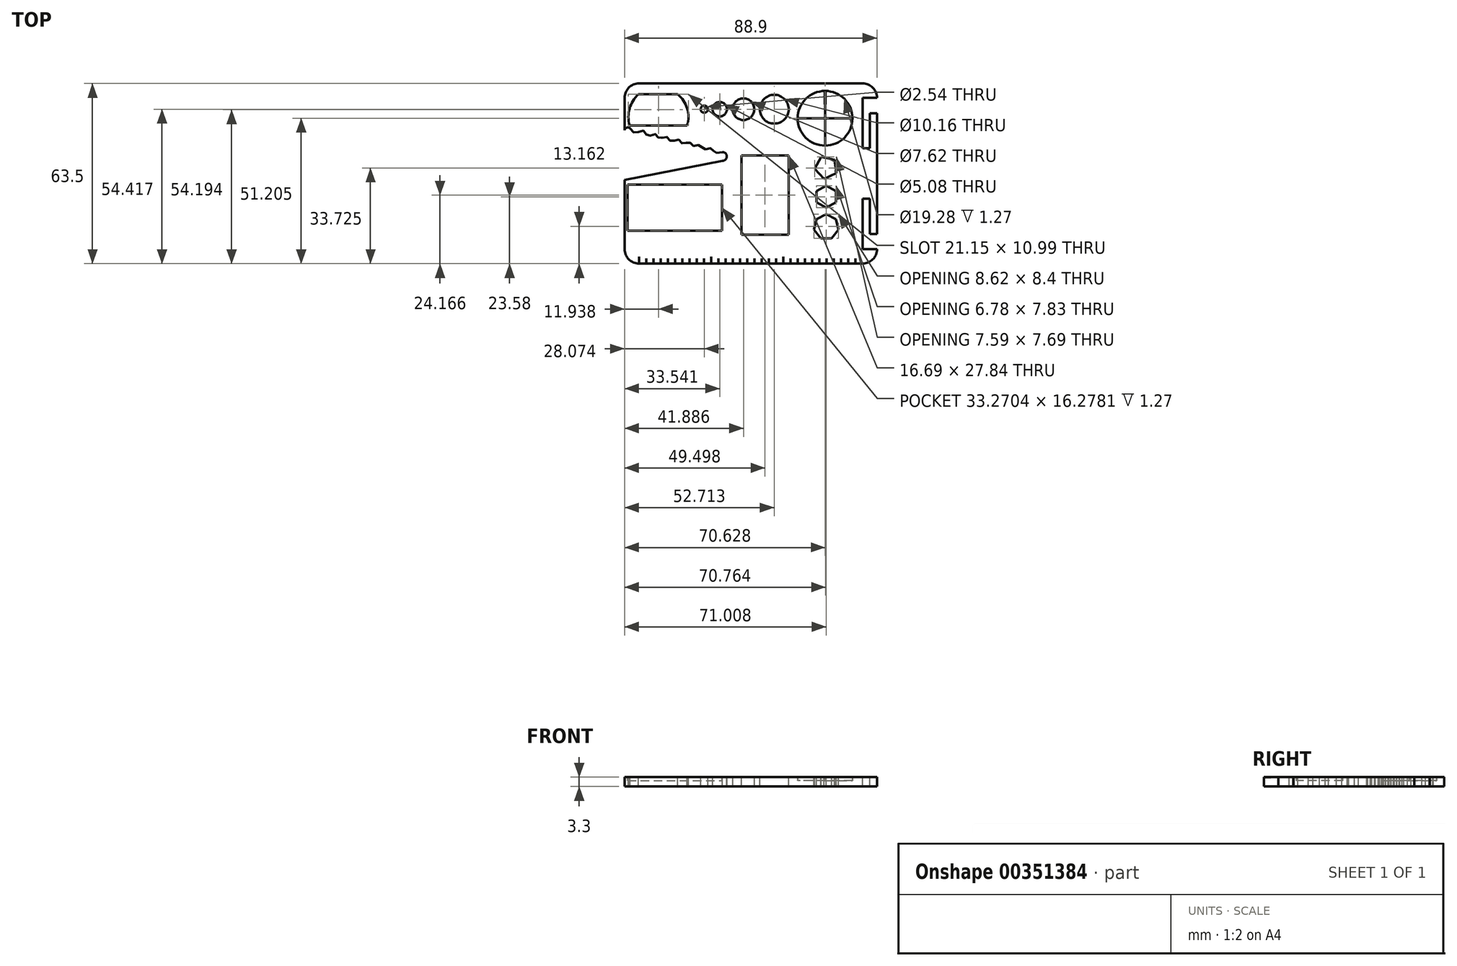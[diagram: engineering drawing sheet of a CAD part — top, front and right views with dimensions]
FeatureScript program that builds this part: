
annotation { "Feature Type Name" : "Feature", "Feature Type Description" : "" }
export const myFeature = defineFeature(function(context is Context, id is Id, definition is map)
    precondition{}
    {
        {
            var Q0;
            Q0=qCreatedBy(makeId("Top.planeOp"),FACE);
            var sketch = newSketch(context, id + "F0", { "sketchPlane" : qUnion([Q0])});
            skLineSegment(sketch, "E0", {"start": v(0, 0) * mm, "end": v(88.9, 0) * mm});
            skLineSegment(sketch, "E1", {"start": v(88.9, 0) * mm, "end": v(88.9, 63.5) * mm});
            skLineSegment(sketch, "E2", {"start": v(88.9, 63.5) * mm, "end": v(0, 63.5) * mm});
            skLineSegment(sketch, "E3", {"start": v(0, 63.5) * mm, "end": v(0, 0) * mm});
            skSolve(sketch);
        }
        {
            var Q0;
            Q0 = qSketchRegion(id + "F0", true);
            extrude(context, id + "F1", {"entities" : qUnion([Q0]), "depth" : 3.3 * mm});
        }
        {
            var Q0;
            Q0=makeQuery(id+"F1.opExtrude","CAP_FACE",FACE,{"disambiguationData":[OSD([sQuery(id+"F0.wireOp",EDGE,"E0"),sQuery(id+"F0.wireOp",EDGE,"E1"),sQuery(id+"F0.wireOp",EDGE,"E2"),sQuery(id+"F0.wireOp",EDGE,"E3")])],"isStart":false});
            var sketch = newSketch(context, id + "F2", { "sketchPlane" : qUnion([Q0])});
            skLineSegment(sketch, "E4", {"start": v(5.08, 0) * mm, "end": v(5.08, 2.43) * mm});
            skLineSegment(sketch, "E5", {"start": v(5.08, 2.43) * mm, "end": v(5.1, 2.43) * mm});
            skLineSegment(sketch, "E6", {"start": v(5.1, 2.43) * mm, "end": v(5.1, 0) * mm});
            skLineSegment(sketch, "E7", {"start": v(5.1, 0) * mm, "end": v(7.65, 0) * mm});
            skLineSegment(sketch, "E8", {"start": v(7.65, 0) * mm, "end": v(7.65, 1.82) * mm});
            skLineSegment(sketch, "E9", {"start": v(0, 0) * mm, "end": v(5.08, 0) * mm});
            skLineSegment(sketch, "E10", {"start": v(7.65, 1.82) * mm, "end": v(7.62, 1.82) * mm});
            skLineSegment(sketch, "E11", {"start": v(7.62, 1.82) * mm, "end": v(7.62, 0) * mm});
            skLineSegment(sketch, "E12", {"start": v(7.62, 0) * mm, "end": v(10.16, 0) * mm});
            skLineSegment(sketch, "E13", {"start": v(10.16, 0) * mm, "end": v(10.16, 1.82) * mm});
            skLineSegment(sketch, "E14", {"start": v(10.16, 1.82) * mm, "end": v(10.19, 1.82) * mm});
            skLineSegment(sketch, "E15", {"start": v(10.19, 1.82) * mm, "end": v(10.19, 0) * mm});
            skLineSegment(sketch, "E16", {"start": v(10.16, 0) * mm, "end": v(12.7, 0) * mm});
            skLineSegment(sketch, "E17", {"start": v(12.7, 0) * mm, "end": v(12.7, 1.82) * mm});
            skLineSegment(sketch, "E18", {"start": v(12.7, 1.82) * mm, "end": v(12.73, 1.82) * mm});
            skLineSegment(sketch, "E19", {"start": v(12.73, 1.82) * mm, "end": v(12.73, 0) * mm});
            skLineSegment(sketch, "E20.0", {"start": v(15.24, 0) * mm, "end": v(15.24, 1.82) * mm});
            skLineSegment(sketch, "E21.0", {"start": v(17.78, 0) * mm, "end": v(17.78, 1.82) * mm});
            skLineSegment(sketch, "E22.0", {"start": v(20.32, 0) * mm, "end": v(20.32, 1.82) * mm});
            skLineSegment(sketch, "E23.0", {"start": v(22.86, 0) * mm, "end": v(22.86, 1.82) * mm});
            skLineSegment(sketch, "E24.0", {"start": v(25.4, 0) * mm, "end": v(25.4, 1.82) * mm});
            skLineSegment(sketch, "E25.0", {"start": v(27.94, 0) * mm, "end": v(27.94, 1.82) * mm});
            skLineSegment(sketch, "E26.0", {"start": v(30.48, 0) * mm, "end": v(30.48, 2.43) * mm});
            skLineSegment(sketch, "E27.0", {"start": v(33.02, 0) * mm, "end": v(33.02, 1.82) * mm});
            skLineSegment(sketch, "E28.0", {"start": v(35.56, 0) * mm, "end": v(35.56, 1.82) * mm});
            skLineSegment(sketch, "E29.0", {"start": v(38.1, 0) * mm, "end": v(38.1, 1.82) * mm});
            skLineSegment(sketch, "E30.0", {"start": v(40.64, 0) * mm, "end": v(40.64, 1.82) * mm});
            skLineSegment(sketch, "E31.0", {"start": v(43.18, 0) * mm, "end": v(43.18, 1.82) * mm});
            skLineSegment(sketch, "E32.0", {"start": v(45.72, 0) * mm, "end": v(45.72, 1.82) * mm});
            skLineSegment(sketch, "E33.0", {"start": v(48.26, 0) * mm, "end": v(48.26, 1.82) * mm});
            skLineSegment(sketch, "E34.0", {"start": v(50.8, 0) * mm, "end": v(50.8, 1.82) * mm});
            skLineSegment(sketch, "E35.0", {"start": v(53.34, 0) * mm, "end": v(53.34, 1.82) * mm});
            skLineSegment(sketch, "E36.0", {"start": v(58.42, 0) * mm, "end": v(58.42, 1.82) * mm});
            skLineSegment(sketch, "E37.0", {"start": v(60.96, 0) * mm, "end": v(60.96, 1.82) * mm});
            skLineSegment(sketch, "E38.0", {"start": v(63.5, 0) * mm, "end": v(63.5, 1.82) * mm});
            skLineSegment(sketch, "E39.0", {"start": v(66.04, 0) * mm, "end": v(66.04, 1.82) * mm});
            skLineSegment(sketch, "E40.0", {"start": v(68.58, 0) * mm, "end": v(68.58, 1.82) * mm});
            skLineSegment(sketch, "E41.0", {"start": v(71.12, 0) * mm, "end": v(71.12, 1.82) * mm});
            skLineSegment(sketch, "E42.0", {"start": v(73.66, 0) * mm, "end": v(73.66, 1.82) * mm});
            skLineSegment(sketch, "E43.0", {"start": v(76.2, 0) * mm, "end": v(76.2, 1.82) * mm});
            skLineSegment(sketch, "E44.0", {"start": v(78.74, 0) * mm, "end": v(78.74, 1.82) * mm});
            skLineSegment(sketch, "E45.0", {"start": v(81.28, 0) * mm, "end": v(81.28, 1.82) * mm});
            skLineSegment(sketch, "E46.0", {"start": v(55.88, 0) * mm, "end": v(55.88, 2.43) * mm});
            skLineSegment(sketch, "E47.0", {"start": v(15.27, 1.82) * mm, "end": v(15.27, 0) * mm});
            skLineSegment(sketch, "E48.0", {"start": v(17.8, 1.82) * mm, "end": v(17.8, 0) * mm});
            skLineSegment(sketch, "E49.0", {"start": v(20.35, 1.82) * mm, "end": v(20.35, 0) * mm});
            skLineSegment(sketch, "E50.0", {"start": v(22.89, 1.82) * mm, "end": v(22.89, 0) * mm});
            skLineSegment(sketch, "E51.0", {"start": v(25.43, 1.82) * mm, "end": v(25.43, 0) * mm});
            skLineSegment(sketch, "E52.0", {"start": v(27.97, 1.82) * mm, "end": v(27.97, 0) * mm});
            skLineSegment(sketch, "E53.0", {"start": v(30.5, 1.82) * mm, "end": v(30.5, 0) * mm});
            skLineSegment(sketch, "E54.0", {"start": v(33.05, 1.82) * mm, "end": v(33.05, 0) * mm});
            skLineSegment(sketch, "E55.0", {"start": v(35.59, 1.82) * mm, "end": v(35.59, 0) * mm});
            skLineSegment(sketch, "E56.0", {"start": v(38.13, 1.82) * mm, "end": v(38.13, 0) * mm});
            skLineSegment(sketch, "E57.0", {"start": v(40.67, 1.82) * mm, "end": v(40.67, 0) * mm});
            skLineSegment(sketch, "E58.0", {"start": v(43.2, 1.82) * mm, "end": v(43.2, 0) * mm});
            skLineSegment(sketch, "E59.0", {"start": v(45.75, 1.82) * mm, "end": v(45.75, 0) * mm});
            skLineSegment(sketch, "E60.0", {"start": v(48.29, 1.82) * mm, "end": v(48.29, 0) * mm});
            skLineSegment(sketch, "E61.0", {"start": v(50.83, 1.82) * mm, "end": v(50.83, 0) * mm});
            skLineSegment(sketch, "E62.0", {"start": v(53.37, 1.82) * mm, "end": v(53.37, 0) * mm});
            skLineSegment(sketch, "E63.0", {"start": v(55.9, 1.82) * mm, "end": v(55.9, 0) * mm});
            skLineSegment(sketch, "E64.0", {"start": v(58.45, 1.82) * mm, "end": v(58.45, 0) * mm});
            skLineSegment(sketch, "E65.0", {"start": v(60.99, 1.82) * mm, "end": v(60.99, 0) * mm});
            skLineSegment(sketch, "E66.0", {"start": v(63.53, 1.82) * mm, "end": v(63.53, 0) * mm});
            skLineSegment(sketch, "E67.0", {"start": v(66.07, 1.82) * mm, "end": v(66.07, 0) * mm});
            skLineSegment(sketch, "E68.0", {"start": v(68.6, 1.82) * mm, "end": v(68.6, 0) * mm});
            skLineSegment(sketch, "E69.0", {"start": v(71.15, 1.82) * mm, "end": v(71.15, 0) * mm});
            skLineSegment(sketch, "E70.0", {"start": v(73.69, 1.82) * mm, "end": v(73.69, 0) * mm});
            skLineSegment(sketch, "E71.0", {"start": v(76.23, 1.82) * mm, "end": v(76.23, 0) * mm});
            skLineSegment(sketch, "E72.0", {"start": v(78.77, 1.82) * mm, "end": v(78.77, 0) * mm});
            skLineSegment(sketch, "E73.0", {"start": v(81.3, 1.82) * mm, "end": v(81.3, 0) * mm});
            skLineSegment(sketch, "E74", {"start": v(15.24, 1.82) * mm, "end": v(15.27, 1.82) * mm});
            skLineSegment(sketch, "E75.trimOffspring", {"start": v(81.28, 1.82) * mm, "end": v(81.3, 1.82) * mm});
            skLineSegment(sketch, "E76.trimOffspring", {"start": v(78.74, 1.82) * mm, "end": v(78.77, 1.82) * mm});
            skLineSegment(sketch, "E77.trimOffspring", {"start": v(76.2, 1.82) * mm, "end": v(76.23, 1.82) * mm});
            skLineSegment(sketch, "E78.trimOffspring", {"start": v(73.66, 1.82) * mm, "end": v(73.69, 1.82) * mm});
            skLineSegment(sketch, "E79.trimOffspring", {"start": v(71.12, 1.82) * mm, "end": v(71.15, 1.82) * mm});
            skLineSegment(sketch, "E80.trimOffspring", {"start": v(68.58, 1.82) * mm, "end": v(68.6, 1.82) * mm});
            skLineSegment(sketch, "E81.trimOffspring", {"start": v(66.04, 1.82) * mm, "end": v(66.07, 1.82) * mm});
            skLineSegment(sketch, "E82.trimOffspring", {"start": v(63.5, 1.82) * mm, "end": v(63.53, 1.82) * mm});
            skLineSegment(sketch, "E83.trimOffspring", {"start": v(60.96, 1.82) * mm, "end": v(60.99, 1.82) * mm});
            skLineSegment(sketch, "E84.trimOffspring", {"start": v(58.42, 1.82) * mm, "end": v(58.45, 1.82) * mm});
            skLineSegment(sketch, "E85", {"start": v(55.9, 1.82) * mm, "end": v(55.9, 2.43) * mm});
            skLineSegment(sketch, "E86", {"start": v(55.9, 2.43) * mm, "end": v(55.88, 2.43) * mm});
            skLineSegment(sketch, "E87.trimOffspring", {"start": v(53.34, 1.82) * mm, "end": v(53.37, 1.82) * mm});
            skLineSegment(sketch, "E88.trimOffspring", {"start": v(50.8, 1.82) * mm, "end": v(50.83, 1.82) * mm});
            skLineSegment(sketch, "E89.trimOffspring", {"start": v(48.26, 1.82) * mm, "end": v(48.29, 1.82) * mm});
            skLineSegment(sketch, "E90.trimOffspring", {"start": v(45.72, 1.82) * mm, "end": v(45.75, 1.82) * mm});
            skLineSegment(sketch, "E91.trimOffspring", {"start": v(43.18, 1.82) * mm, "end": v(43.2, 1.82) * mm});
            skLineSegment(sketch, "E92.trimOffspring", {"start": v(40.64, 1.82) * mm, "end": v(40.67, 1.82) * mm});
            skLineSegment(sketch, "E93.trimOffspring", {"start": v(38.1, 1.82) * mm, "end": v(38.13, 1.82) * mm});
            skLineSegment(sketch, "E94.trimOffspring", {"start": v(35.56, 1.82) * mm, "end": v(35.59, 1.82) * mm});
            skLineSegment(sketch, "E95.trimOffspring", {"start": v(33.02, 1.82) * mm, "end": v(33.05, 1.82) * mm});
            skLineSegment(sketch, "E96.trimOffspring", {"start": v(17.78, 1.82) * mm, "end": v(17.8, 1.82) * mm});
            skLineSegment(sketch, "E97.trimOffspring", {"start": v(20.32, 1.82) * mm, "end": v(20.35, 1.82) * mm});
            skLineSegment(sketch, "E98.trimOffspring", {"start": v(22.86, 1.82) * mm, "end": v(22.89, 1.82) * mm});
            skLineSegment(sketch, "E99.trimOffspring", {"start": v(27.94, 1.82) * mm, "end": v(27.97, 1.82) * mm});
            skLineSegment(sketch, "E100", {"start": v(30.48, 2.43) * mm, "end": v(30.5, 2.43) * mm});
            skLineSegment(sketch, "E101", {"start": v(30.5, 2.43) * mm, "end": v(30.5, 1.82) * mm});
            skLineSegment(sketch, "E102", {"start": v(5.08, 0) * mm, "end": v(81.3, 0) * mm});
            skLineSegment(sketch, "E103", {"start": v(25.4, 1.82) * mm, "end": v(25.43, 1.82) * mm});
            skLineSegment(sketch, "E104", {"start": v(4.86, 59.7) * mm, "end": v(18.65, 59.7) * mm});
            skArc(sketch, "E105", {"start": v(22.06, 48.7) * mm, "mid": v(22.05, 54.72) * mm, "end": v(18.65, 59.7) * mm});
            skArc(sketch, "E106", {"start": v(4.86, 59.7) * mm, "mid": v(1.77, 54.63) * mm, "end": v(1.78, 48.7) * mm});
            skLineSegment(sketch, "E107", {"start": v(1.78, 48.7) * mm, "end": v(22.06, 48.7) * mm});
            skSolve(sketch);
        }
        {
            var Q0;
            Q0=makeQuery(id+"F1.opExtrude","SWEPT_EDGE",EDGE,{"disambiguationData":[OSD([sQuery(id+"F0.wireOp",EDGE,"E0"),sQuery(id+"F0.wireOp",EDGE,"E3")])]});
            var Q1;
            Q1=makeQuery(id+"F1.opExtrude","SWEPT_EDGE",EDGE,{"disambiguationData":[OSD([sQuery(id+"F0.wireOp",EDGE,"E0"),sQuery(id+"F0.wireOp",EDGE,"E1")])]});
            var Q2;
            Q2=makeQuery(id+"F1.opExtrude","SWEPT_EDGE",EDGE,{"disambiguationData":[OSD([sQuery(id+"F0.wireOp",EDGE,"E1"),sQuery(id+"F0.wireOp",EDGE,"E2")])]});
            var Q3;
            Q3=makeQuery(id+"F1.opExtrude","SWEPT_EDGE",EDGE,{"disambiguationData":[OSD([sQuery(id+"F0.wireOp",EDGE,"E2"),sQuery(id+"F0.wireOp",EDGE,"E3")])]});
            fillet(context, id + "F3", {"entities" : qUnion([Q0, Q1, Q2, Q3]), "radius" : 5.08 * mm, "tangentPropagation" : true, "allowEdgeOverflow" : false});
        }
        {
            var Q0;
            Q0 = qSketchRegion(id + "F2", true);
            extrude(context, id + "F4", {"entities" : qUnion([Q0]), "operationType" : NewBodyOperationType.REMOVE, "oppositeDirection" : true, "depth" : 0.25 * mm});
        }
        {
            var Q0;
            Q0=makeQuery(id+"F1.opExtrude","CAP_FACE",FACE,{"disambiguationData":[OSD([sQuery(id+"F0.wireOp",EDGE,"E0"),sQuery(id+"F0.wireOp",EDGE,"E1"),sQuery(id+"F0.wireOp",EDGE,"E2"),sQuery(id+"F0.wireOp",EDGE,"E3")])],"isStart":false});
            var sketch = newSketch(context, id + "F5", { "sketchPlane" : qUnion([Q0])});
            skCircle(sketch, "E108", {"center": v(28.07, 54.42) * mm, "radius": 1.27 * mm});
            skCircle(sketch, "E109", {"center": v(33.54, 54.42) * mm, "radius": 2.54 * mm});
            skCircle(sketch, "E110", {"center": v(41.89, 54.42) * mm, "radius": 3.81 * mm});
            skCircle(sketch, "E111", {"center": v(52.71, 54.42) * mm, "radius": 5.08 * mm});
            skArc(sketch, "E112.0", {"start": v(4.86, 59.7) * mm, "mid": v(1.77, 54.63) * mm, "end": v(1.78, 48.7) * mm});
            skLineSegment(sketch, "E113.0", {"start": v(4.86, 59.7) * mm, "end": v(18.65, 59.7) * mm});
            skArc(sketch, "E114.0", {"start": v(22.06, 48.7) * mm, "mid": v(22.05, 54.72) * mm, "end": v(18.65, 59.7) * mm});
            skLineSegment(sketch, "E115.0", {"start": v(1.78, 48.7) * mm, "end": v(22.06, 48.7) * mm});
            skSolve(sketch);
        }
        {
            var Q0;
            Q0 = qSketchRegion(id + "F5", true);
            extrude(context, id + "F6", {"entities" : qUnion([Q0]), "operationType" : NewBodyOperationType.REMOVE, "oppositeDirection" : true, "depth" : 25.4 * mm});
        }
        {
            var Q0;
            Q0=makeQuery(id+"F1.opExtrude","SWEPT_FACE",FACE,{"disambiguationData":[OSD([sQuery(id+"F0.wireOp",EDGE,"E1")])]});
            var sketch = newSketch(context, id + "F7", { "sketchPlane" : qUnion([Q0])});
            skLineSegment(sketch, "E116.0", {"start": v(5.08, 3.3) * mm, "end": v(5.08, 0) * mm});
            skLineSegment(sketch, "E117.0", {"start": v(5.08, 3.3) * mm, "end": v(58.42, 3.3) * mm});
            skLineSegment(sketch, "E118.0", {"start": v(58.42, 0) * mm, "end": v(58.42, 3.3) * mm});
            skLineSegment(sketch, "E119.0", {"start": v(5.08, 0) * mm, "end": v(58.42, 0) * mm});
            skSolve(sketch);
        }
        {
            var Q0;
            Q0 = qSketchRegion(id + "F7", true);
            extrude(context, id + "F8", {"entities" : qUnion([Q0]), "operationType" : NewBodyOperationType.REMOVE, "oppositeDirection" : true, "depth" : 5.08 * mm});
        }
        {
            var Q0;
            Q0=makeQuery(id+"F8.boolean.opBoolean","COPY",FACE,{"derivedFrom":makeQuery(id+"F8.opExtrude","CAP_FACE",FACE,{"disambiguationData":[OSD([sQuery(id+"F7.wireOp",EDGE,"E116.0"),sQuery(id+"F7.wireOp",EDGE,"E117.0"),sQuery(id+"F7.wireOp",EDGE,"E118.0"),sQuery(id+"F7.wireOp",EDGE,"E119.0")])],"isStart":false})});
            var sketch = newSketch(context, id + "F9", { "sketchPlane" : qUnion([Q0])});
            skPoint(sketch, "E120.startSnap0", {"position": v(5.08, 1.65) * mm});
            skPoint(sketch, "E120.startSnap1", {"position": v(31.75, 0) * mm});
            skLineSegment(sketch, "E121", {"start": v(22.86, 0) * mm, "end": v(22.86, 3.3) * mm});
            skLineSegment(sketch, "E122", {"start": v(40.64, 3.3) * mm, "end": v(22.86, 3.3) * mm});
            skLineSegment(sketch, "E123", {"start": v(40.64, 3.3) * mm, "end": v(40.64, 0) * mm});
            skLineSegment(sketch, "E124", {"start": v(40.64, 0) * mm, "end": v(22.86, 0) * mm});
            skSolve(sketch);
        }
        {
            var Q0;
            Q0 = qSketchRegion(id + "F9", true);
            extrude(context, id + "F10", {"entities" : qUnion([Q0]), "operationType" : NewBodyOperationType.ADD, "depth" : 2.54 * mm});
        }
        {
            var Q0;
            {var subQ0=sQuery(id+"F0.wireOp",EDGE,"E3");var subQ1=sQuery(id+"F0.wireOp",EDGE,"E2");var subQ2=sQuery(id+"F0.wireOp",EDGE,"E1");Q0=makeQuery(id+"Fheyj9GnmQKfGOX_1.boolean.opBoolean","SPLIT",FACE,{"disambiguationData":[TD([makeQuery(id+"F1.opExtrude","SWEPT_FACE",FACE,{"disambiguationData":[OSD([subQ1])]})])],"derivedFrom":makeQuery(id+"F1.opExtrude","CAP_FACE",FACE,{"disambiguationData":[OSD([sQuery(id+"F0.wireOp",EDGE,"E0"),subQ2,subQ1,subQ0])],"isStart":false})});}
            var sketch = newSketch(context, id + "F11", { "sketchPlane" : qUnion([Q0])});
            skLineSegment(sketch, "E125", {"start": v(34.47, 36.23) * mm, "end": v(0, 29.44) * mm});
            skArc(sketch, "E126", {"start": v(34.47, 36.23) * mm, "mid": v(36.01, 37.77) * mm, "end": v(34.47, 39.32) * mm});
            skFitSpline(sketch, "E127", {"points": [v(34.47, 39.32) * mm, v(31.6, 39.32) * mm, v(30.46, 40.69) * mm, v(27.95, 40.38) * mm, v(26.5, 41.74) * mm, v(24.3, 41.5) * mm, v(22.66, 42.85) * mm, v(20.42, 42.29) * mm, v(18.81, 43.75) * mm, v(16.53, 42.98) * mm, v(14.76, 44.7) * mm, v(12.26, 44.12) * mm, v(10.92, 45.6) * mm, v(8.2, 44.96) * mm, v(6.7, 46.8) * mm, v(3.93, 46.06) * mm, v(1.95, 47.66) * mm], "startDerivative": vector(-49.51, -10.48) * mm, "endDerivative": vector(-26.38, 38.01) * mm});
            skArc(sketch, "E128", {"start": v(1.95, 47.66) * mm, "mid": v(0.77, 47.9) * mm, "end": v(0, 46.96) * mm});
            skLineSegment(sketch, "E129", {"start": v(0, 46.96) * mm, "end": v(0, 29.44) * mm});
            skSolve(sketch);
        }
        {
            var Q0;
            Q0 = qSketchRegion(id + "F11", true);
            extrude(context, id + "F12", {"entities" : qUnion([Q0]), "operationType" : NewBodyOperationType.REMOVE, "oppositeDirection" : true, "depth" : 25.4 * mm});
        }
        {
            var Q0;
            {var subQ9=sQuery(id+"F0.wireOp",EDGE,"E3");var subQ10=sQuery(id+"F0.wireOp",EDGE,"E2");var subQ13=makeQuery(id+"F1.opExtrude","SWEPT_FACE",FACE,{"disambiguationData":[OSD([subQ10])]});var subQ18=sQuery(id+"F0.wireOp",EDGE,"E1");Q0=makeQuery(id+"FrTG45sfuEWpLZh_1.boolean.opBoolean","SPLIT",FACE,{"disambiguationData":[TD([subQ13])],"derivedFrom":makeQuery(id+"Fheyj9GnmQKfGOX_1.boolean.opBoolean","SPLIT",FACE,{"disambiguationData":[TD([subQ13])],"derivedFrom":makeQuery(id+"F1.opExtrude","CAP_FACE",FACE,{"disambiguationData":[OSD([sQuery(id+"F0.wireOp",EDGE,"E0"),subQ18,subQ10,subQ9])],"isStart":false})})});}
            var sketch = newSketch(context, id + "F13", { "sketchPlane" : qUnion([Q0])});
            skCircle(sketch, "E130", {"center": v(70.63, 51.2) * mm, "radius": 9.64 * mm});
            skLineSegment(sketch, "E131", {"start": v(70.63, 51.2) * mm, "end": v(80.27, 51.27) * mm});
            skLineSegment(sketch, "E132", {"start": v(70.63, 51.2) * mm, "end": v(80.27, 51.15) * mm});
            skLineSegment(sketch, "E133", {"start": v(70.63, 51.2) * mm, "end": v(70.53, 60.84) * mm});
            skLineSegment(sketch, "E134", {"start": v(70.63, 51.2) * mm, "end": v(70.73, 60.84) * mm});
            skLineSegment(sketch, "E135", {"start": v(70.63, 51.2) * mm, "end": v(70.6, 41.57) * mm});
            skLineSegment(sketch, "E136", {"start": v(70.63, 51.2) * mm, "end": v(70.66, 41.57) * mm});
            skLineSegment(sketch, "E137", {"start": v(70.63, 51.2) * mm, "end": v(60.99, 51.28) * mm});
            skLineSegment(sketch, "E138", {"start": v(70.63, 51.2) * mm, "end": v(60.99, 51.14) * mm});
            skSolve(sketch);
        }
        {
            var Q0;
            Q0 = qSketchRegion(id + "F13", true);
            extrude(context, id + "F14", {"entities" : qUnion([Q0]), "operationType" : NewBodyOperationType.REMOVE, "oppositeDirection" : true, "depth" : 1.27 * mm});
        }
        {
            var Q0;
            Q0=makeQuery(id+"F14.boolean.opBoolean","COPY",FACE,{"derivedFrom":makeQuery(id+"F14.opExtrude","CAP_FACE",FACE,{"disambiguationData":[OSD([sQuery(id+"F13.wireOp",EDGE,"E130")])],"isStart":false})});
            var sketch = newSketch(context, id + "F15", { "sketchPlane" : qUnion([Q0])});
            skLineSegment(sketch, "E139.0", {"start": v(70.63, 51.2) * mm, "end": v(70.53, 60.84) * mm});
            skLineSegment(sketch, "E140.0", {"start": v(70.63, 51.2) * mm, "end": v(70.73, 60.84) * mm});
            skLineSegment(sketch, "E141.0", {"start": v(70.63, 51.2) * mm, "end": v(80.27, 51.27) * mm});
            skLineSegment(sketch, "E142.0", {"start": v(70.63, 51.2) * mm, "end": v(80.27, 51.15) * mm});
            skLineSegment(sketch, "E143.0", {"start": v(70.63, 51.2) * mm, "end": v(60.99, 51.28) * mm});
            skLineSegment(sketch, "E144.0", {"start": v(70.63, 51.2) * mm, "end": v(60.99, 51.14) * mm});
            skLineSegment(sketch, "E145.0", {"start": v(70.63, 51.2) * mm, "end": v(70.66, 41.57) * mm});
            skLineSegment(sketch, "E146.0", {"start": v(70.63, 51.2) * mm, "end": v(70.6, 41.57) * mm});
            skLineSegment(sketch, "E147", {"start": v(70.53, 60.84) * mm, "end": v(70.73, 60.84) * mm});
            skLineSegment(sketch, "E148", {"start": v(80.26, 51.27) * mm, "end": v(80.26, 51.15) * mm});
            skLineSegment(sketch, "E149", {"start": v(70.53, 60.82) * mm, "end": v(70.73, 60.82) * mm});
            skLineSegment(sketch, "E150", {"start": v(61, 51.28) * mm, "end": v(61, 51.14) * mm});
            skLineSegment(sketch, "E151", {"start": v(70.6, 41.57) * mm, "end": v(70.66, 41.57) * mm});
            skSolve(sketch);
        }
        {
            var Q0;
            Q0 = qSketchRegion(id + "F15", true);
            extrude(context, id + "F16", {"entities" : qUnion([Q0]), "depth" : 1.27 * mm});
        }
        {
            var Q0;
            {var subQ0=sQuery(id+"F0.wireOp",EDGE,"E2");Q0=makeQuery(id+"F13.imprint","IMPRINT",FACE,{"disambiguationData":[TD([[makeQuery(id+"F13.imprint","IMPRINT",EDGE,{"derivedFrom":makeQuery(id+"F1.opExtrude","CAP_EDGE",EDGE,{"disambiguationData":[OSD([subQ0])],"isStart":false})}),1.0]])]});}
            var sketch = newSketch(context, id + "F17", { "sketchPlane" : qUnion([Q0])});
            skLineSegment(sketch, "E152", {"start": v(41.16, 38.09) * mm, "end": v(41.16, 10.24) * mm});
            skLineSegment(sketch, "E153", {"start": v(41.16, 10.24) * mm, "end": v(57.84, 10.24) * mm});
            skLineSegment(sketch, "E154", {"start": v(41.16, 38.09) * mm, "end": v(57.84, 38.09) * mm});
            skLineSegment(sketch, "E155", {"start": v(57.84, 38.09) * mm, "end": v(57.84, 10.24) * mm});
            skCircle(sketch, "E156.cCircle", {"center": v(71, 33.87) * mm, "radius": 4.07 * mm, "construction": true});
            skLineSegment(sketch, "E156.0", {"start": v(74.56, 31.89) * mm, "end": v(70.22, 29.88) * mm});
            skLineSegment(sketch, "E156.1", {"start": v(70.22, 29.88) * mm, "end": v(66.97, 33.4) * mm});
            skLineSegment(sketch, "E156.2", {"start": v(66.97, 33.4) * mm, "end": v(69.3, 37.57) * mm});
            skLineSegment(sketch, "E156.3", {"start": v(69.3, 37.57) * mm, "end": v(74, 36.64) * mm});
            skLineSegment(sketch, "E156.4", {"start": v(74, 36.64) * mm, "end": v(74.56, 31.89) * mm});
            skCircle(sketch, "E157.cCircle", {"center": v(71, 23.58) * mm, "radius": 3.91 * mm, "construction": true});
            skLineSegment(sketch, "E157.0", {"start": v(71, 27.5) * mm, "end": v(74.4, 25.54) * mm});
            skLineSegment(sketch, "E157.1", {"start": v(74.4, 25.54) * mm, "end": v(74.4, 21.62) * mm});
            skLineSegment(sketch, "E157.2", {"start": v(74.4, 21.62) * mm, "end": v(71, 19.67) * mm});
            skLineSegment(sketch, "E157.3", {"start": v(71, 19.67) * mm, "end": v(67.62, 21.62) * mm});
            skLineSegment(sketch, "E157.4", {"start": v(67.62, 21.62) * mm, "end": v(67.62, 25.54) * mm});
            skLineSegment(sketch, "E157.5", {"start": v(67.62, 25.54) * mm, "end": v(71, 27.5) * mm});
            skCircle(sketch, "E158.cCircle", {"center": v(71, 12.94) * mm, "radius": 4.42 * mm, "construction": true});
            skLineSegment(sketch, "E158.0", {"start": v(71, 17.36) * mm, "end": v(74.46, 15.7) * mm});
            skLineSegment(sketch, "E158.1", {"start": v(74.46, 15.7) * mm, "end": v(75.32, 11.96) * mm});
            skLineSegment(sketch, "E158.2", {"start": v(75.32, 11.96) * mm, "end": v(72.93, 8.96) * mm});
            skLineSegment(sketch, "E158.3", {"start": v(72.93, 8.96) * mm, "end": v(69.1, 8.96) * mm});
            skLineSegment(sketch, "E158.4", {"start": v(69.1, 8.96) * mm, "end": v(66.7, 11.96) * mm});
            skLineSegment(sketch, "E158.5", {"start": v(66.7, 11.96) * mm, "end": v(67.55, 15.7) * mm});
            skLineSegment(sketch, "E158.6", {"start": v(67.55, 15.7) * mm, "end": v(71, 17.36) * mm});
            skSolve(sketch);
        }
        {
            var Q0;
            Q0 = qSketchRegion(id + "F17", true);
            extrude(context, id + "F18", {"entities" : qUnion([Q0]), "operationType" : NewBodyOperationType.REMOVE, "oppositeDirection" : true, "depth" : 25.4 * mm});
        }
        {
            var Q0;
            {var subQ0=sQuery(id+"F0.wireOp",EDGE,"E2");Q0=makeQuery(id+"F13.imprint","IMPRINT",FACE,{"disambiguationData":[TD([[makeQuery(id+"F13.imprint","IMPRINT",EDGE,{"derivedFrom":makeQuery(id+"F1.opExtrude","CAP_EDGE",EDGE,{"disambiguationData":[OSD([subQ0])],"isStart":false})}),1.0]])]});}
            var sketch = newSketch(context, id + "F19", { "sketchPlane" : qUnion([Q0])});
            skLineSegment(sketch, "E159", {"start": v(1.08, 27.83) * mm, "end": v(34.35, 27.83) * mm});
            skLineSegment(sketch, "E160", {"start": v(34.35, 27.83) * mm, "end": v(34.35, 11.55) * mm});
            skLineSegment(sketch, "E161", {"start": v(34.35, 11.55) * mm, "end": v(1.08, 11.55) * mm});
            skLineSegment(sketch, "E162", {"start": v(1.08, 27.83) * mm, "end": v(1.08, 11.55) * mm});
            skPoint(sketch, "E163.orphan", {"position": v(0, 27.83) * mm});
            skPoint(sketch, "E164.orphan", {"position": v(0, 11.55) * mm});
            skSolve(sketch);
        }
        {
            var Q0;
            Q0 = qSketchRegion(id + "F19", true);
            extrude(context, id + "F20", {"entities" : qUnion([Q0]), "operationType" : NewBodyOperationType.REMOVE, "oppositeDirection" : true, "depth" : 1.27 * mm});
        }
        {
            var Q0;
            Q0=makeQuery(id+"F10.opExtrude","CAP_FACE",FACE,{"disambiguationData":[OSD([sQuery(id+"F9.wireOp",EDGE,"E121"),sQuery(id+"F9.wireOp",EDGE,"E122"),sQuery(id+"F9.wireOp",EDGE,"E123"),sQuery(id+"F9.wireOp",EDGE,"E124")])],"isStart":false});
            var sketch = newSketch(context, id + "F21", { "sketchPlane" : qUnion([Q0])});
            skLineSegment(sketch, "E165", {"start": v(22.86, 3.3) * mm, "end": v(10.47, 3.3) * mm});
            skLineSegment(sketch, "E166", {"start": v(10.47, 3.3) * mm, "end": v(10.47, 0) * mm});
            skLineSegment(sketch, "E167", {"start": v(10.47, 0) * mm, "end": v(22.86, 0) * mm});
            skLineSegment(sketch, "E168", {"start": v(22.86, 0) * mm, "end": v(40.64, 0) * mm});
            skLineSegment(sketch, "E169", {"start": v(40.64, 0) * mm, "end": v(53.04, 0) * mm});
            skLineSegment(sketch, "E170", {"start": v(53.04, 0) * mm, "end": v(53.04, 3.3) * mm});
            skLineSegment(sketch, "E171", {"start": v(53.04, 3.3) * mm, "end": v(40.64, 3.3) * mm});
            skLineSegment(sketch, "E172", {"start": v(40.64, 3.3) * mm, "end": v(22.86, 3.3) * mm});
            skSolve(sketch);
        }
        {
            var Q0;
            Q0 = qSketchRegion(id + "F21", true);
            extrude(context, id + "F22", {"entities" : qUnion([Q0]), "operationType" : NewBodyOperationType.ADD, "depth" : 2.54 * mm});
        }
    });
